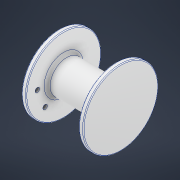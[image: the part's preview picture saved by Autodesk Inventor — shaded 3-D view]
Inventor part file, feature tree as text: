
AUTODESK INVENTOR PART (.ipt)
format: ipt  version: 2021 (Build 250183000, 183)  size: 195,584 bytes
history: native  units: mm
features: sketch x3, fillet x2, revolve x1, hole x1, extrude x1, chamfer x1
ambient origin geometry x8: Origin, YZ Plane, XZ Plane, XY Plane, X Axis, Y Axis, Z Axis, Center Point
bodies: Solid1 (feature_tree)
feature tree (9):
  revolve  "Revolution1"  [1 undecoded]
  hole  "Hole1"  [1 undecoded]
  extrude  "Extrusion1"  Depth=0.5mm
  chamfer  "Chamfer1"  Distance=3.0mm
  fillet  "Fillet1"  Radius=1.3mm
  fillet  "Fillet2"  Radius=22.0mm
  sketch  "Sketch1"  dims[d0=3.0mm d1=11.0mm]
  sketch  "Sketch2"  dims[d2=25.0mm d3=17.5mm]
  sketch  "Sketch3"  dims[d4=90.0deg d5=3.0mm d6=6.0mm d7=4.0mm d8=2.0mm d9=90.0deg d10=8.0mm d11=20.594885mm d12=7.0mm d13=3.0mm d14=1.3mm d15=22.0mm d16=0.0mm d17=0.5mm d18=2.0mm d19=45.0deg d20=2.0mm d21=0.5mm d23=17.5mm d24=17.5mm d25=45.0deg]
note: 2 required parameter values undecoded (feature->parameter linkage not recoverable at this tier; creation-order binding heuristic only, values carry confidence <= 0.55)